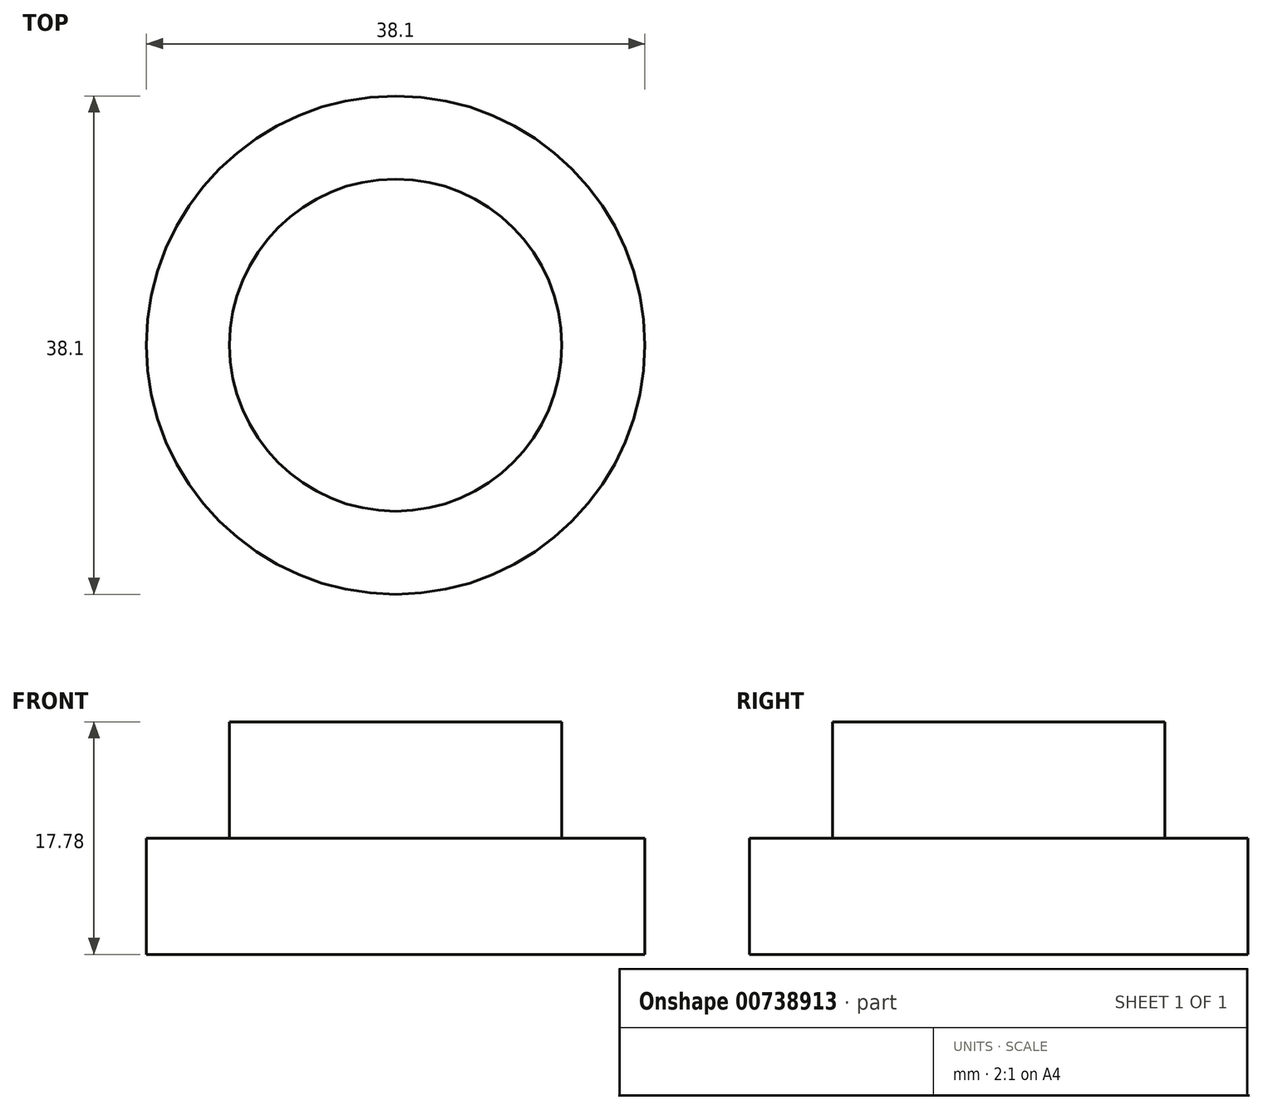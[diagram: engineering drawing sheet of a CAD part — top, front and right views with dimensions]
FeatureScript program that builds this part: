
annotation { "Feature Type Name" : "Feature", "Feature Type Description" : "" }
export const myFeature = defineFeature(function(context is Context, id is Id, definition is map)
    precondition{}
    {
        {
            var Q0;
            Q0=qCreatedBy(makeId("Top.planeOp"),FACE);
            var sketch = newSketch(context, id + "F0", { "sketchPlane" : qUnion([Q0])});
            skCircle(sketch, "E0", {"center": v(0, 0) * mm, "radius": 19.05 * mm});
            skSolve(sketch);
        }
        {
            var Q0;
            Q0=makeQuery(id+"F0.imprint","IMPRINT",FACE,{"disambiguationData":[TD([[makeQuery(id+"F0.imprint","IMPRINT",EDGE,{"derivedFrom":sQuery(id+"F0.wireOp",EDGE,"E0")}),1.0]])]});
            extrude(context, id + "F1", {"entities" : qUnion([Q0]), "depth" : 8.9 * mm, "offsetDistance" : 25.4 * mm});
        }
        {
            var Q0;
            Q0=makeQuery(id+"F1.opExtrude","CAP_FACE",FACE,{"disambiguationData":[OSD([sQuery(id+"F0.wireOp",EDGE,"E0")])],"isStart":true});
            var sketch = newSketch(context, id + "F2", { "sketchPlane" : qUnion([Q0])});
            skCircle(sketch, "E1", {"center": v(0, 0) * mm, "radius": 12.7 * mm});
            skSolve(sketch);
        }
        {
            var Q0;
            Q0 = qSketchRegion(id + "F2", true);
            extrude(context, id + "F3", {"entities" : qUnion([Q0]), "operationType" : NewBodyOperationType.ADD, "oppositeDirection" : true, "depth" : 17.78 * mm, "offsetDistance" : 25.4 * mm});
        }
    });
